# Revit family: LB6LEDA
name_source: partatom
category: Lighting Fixtures
revit_build: Autodesk Revit 2014 (Build: 20130308_1515(x64)
units: mm (PartAtom-declared; Revit-internal decimal feet)

## types (1)
- LB6LEDA
    Apparent Load = 13 VA
    Assembly Code = D5020200
    Color Filter = 16777215
    Connector Description = Lighting Connector
    Default Elevation = 48"
    Description = Performs like 65W BR30 or 18W compact fluorescent, using only 13.5 watts of power. LB6LEDA features excellent glare control and optical cutoff, color quality and a warm white color temperature.
    Dimming Lamp Color Temperature Shift = <None>
    Drum-Height = 24"
    Emit Shape Visible in Rendering = No
    Emit from Circle Diameter = 6"
    Features = •	12-13 watt input power
•	ENERGY STAR® Qualified (WH)
•	New Construction with DBXQL housing; can be used to meet California Title 24 requirements for commercial buildings
•	Retrofit applications with compatible 6 inch housings from Prescolite or others using the universal screw base adapter
•	Photometric testing per IESNA LM-79 2008 standards
•	Lumen output and distribution comparable up to a 75W PAR incandescent lamp or a 26 watt CFL lamp
•	Dimmable to 15% with most standard dimmers
•	Easy installation with (3) friction spring clips and diffuse polycarbonate lens controls direct glare
•	Up to 60,000 hours at 70% lumen maintenance per TM-21
•	Integral Aluminum heat sink to maximize life expectancy and lumen output
•	UL/cUL classified or cCSAus listed in Prescolite and many competitive housings
•	Suitable for wet locations
    Fixture distribution = Direct
    Housing Material = Paint - Hubbell - Matte White
    Lamp = LED
    Load Classification = Lighting
    Manufacturer = Whiteway
    Model = LB6LEDA
    Photometric Web File = generic
    Power Factor = 1
    Product Documentation Link = https://hubbellcdn.com
    Product Link = https://www.hubbell.com
    Reflector Finish = Hubbell - White Glass
    Tilt Angle = 60.00°
    URL = https://www.hubbell.com
    Voltage = 120 V
    Warranty = 5 years Warranty
    Wattage Comments = 13W
    Watts = 13 W
    Wings = Paint - Hubbell - Light Silver

## geometry (parser evidence)
native form markers: Blend x15, Sweep x1
no freeform markers — native parametric forms only
